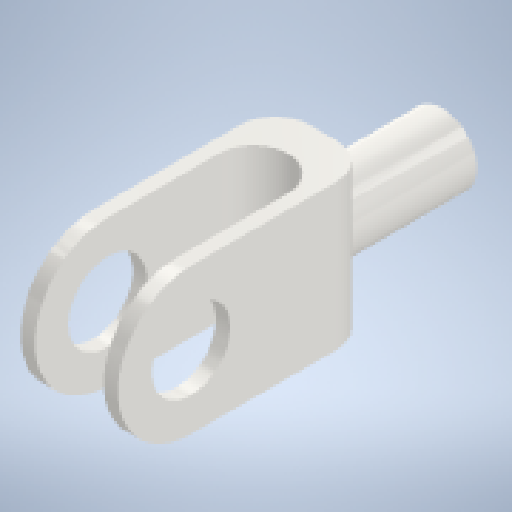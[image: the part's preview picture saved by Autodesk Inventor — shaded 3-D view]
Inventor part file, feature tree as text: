
AUTODESK INVENTOR PART (.ipt)
format: ipt  version: 2024 (Build 280153000, 153)  size: 329,728 bytes
history: native  units: mm
features: extrude x4, sketch x4, other x3, fillet x2
ambient origin geometry x8: Origin, YZ Plane, XZ Plane, XY Plane, X Axis, Y Axis, Z Axis, Center Point
bodies: Solid1 (feature_tree)
feature tree (13):
  extrude  "Extrusion1"  Depth=33.0mm
  extrude  "Extrusion2"  Depth=66.0mm
  extrude  "Extrusion3"  Depth=50.0mm TaperAngle=0.0deg
  other  "Full Round Fillet1"
  other  "Full Round Fillet2"
  extrude  "Extrusion4"  Depth=2.0mm
  other  "Full Round Fillet3"
  fillet  "Fillet1"  Radius=30.6mm
  fillet  "Fillet2"  Radius=20.5mm
  sketch  "Sketch1"  dims[d0=29.0mm d1=33.0mm]
  sketch  "Sketch2"  dims[d2=52.0mm d3=66.0mm]
  sketch  "Sketch3"  dims[d4=26.0mm d5=50.0mm d6=0.0mm]
  sketch  "Sketch4"  dims[d7=41.0mm d8=61.2mm d9=30.6mm d10=20.5mm d11=15.0mm d12=0.0mm d13=6.0mm d15=6.0mm d16=91.8mm d17=0.0mm d18=33.0mm d19=30.6mm d20=30.6mm d21=50.0mm d22=0.0mm d23=15.0mm d24=2.0mm]
